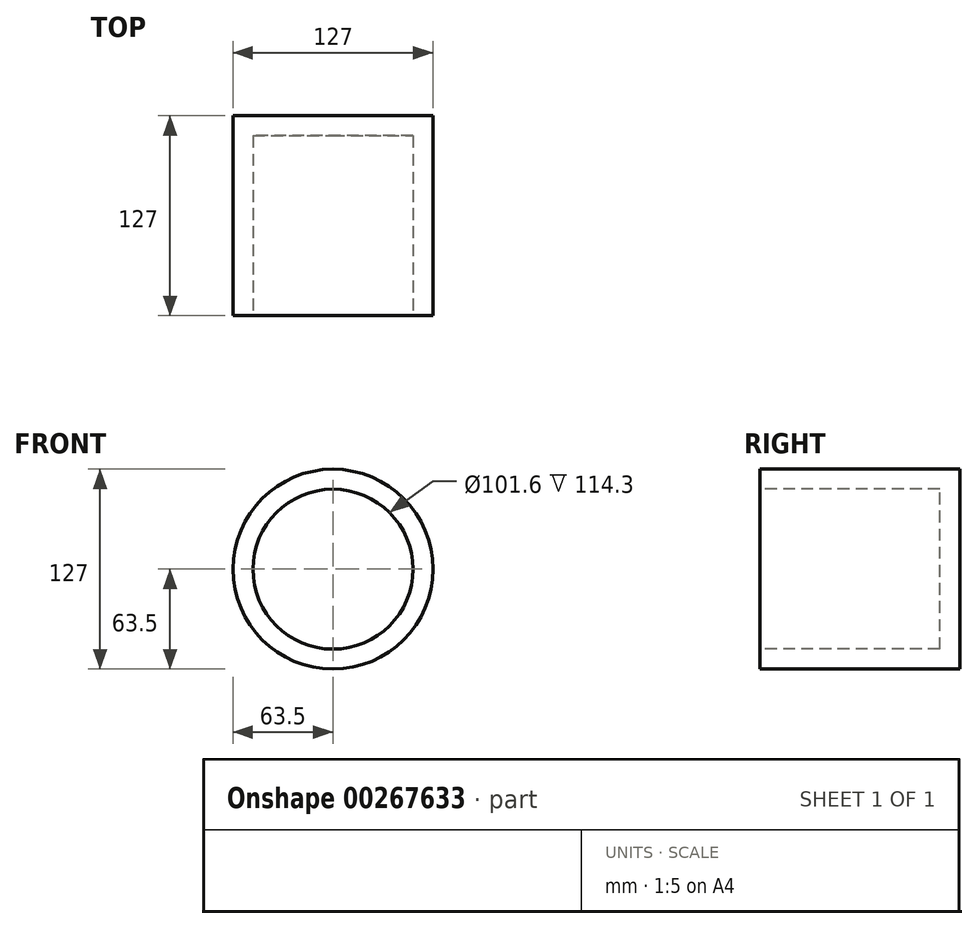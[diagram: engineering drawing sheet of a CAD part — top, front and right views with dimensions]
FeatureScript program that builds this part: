
annotation { "Feature Type Name" : "Feature", "Feature Type Description" : "" }
export const myFeature = defineFeature(function(context is Context, id is Id, definition is map)
    precondition{}
    {
        {
            var Q0;
            Q0=qCreatedBy(makeId("Front.planeOp"),FACE);
            var sketch = newSketch(context, id + "F0", { "sketchPlane" : qUnion([Q0])});
            skCircle(sketch, "E0", {"center": v(0, 0) * mm, "radius": 63.5 * mm});
            skCircle(sketch, "E1", {"center": v(0, 0) * mm, "radius": 50.8 * mm});
            skSolve(sketch);
        }
        {
            var Q0;
            Q0=makeQuery(id+"F0.imprint","IMPRINT",FACE,{"disambiguationData":[TD([[makeQuery(id+"F0.imprint","IMPRINT",EDGE,{"derivedFrom":sQuery(id+"F0.wireOp",EDGE,"E0")}),1.0]])]});
            var Q1;
            Q1=makeQuery(id+"F0.imprint","IMPRINT",FACE,{"disambiguationData":[TD([[makeQuery(id+"F0.imprint","IMPRINT",EDGE,{"derivedFrom":sQuery(id+"F0.wireOp",EDGE,"E1")}),1.0]])]});
            extrude(context, id + "F1", {"entities" : qUnion([Q0, Q1]), "oppositeDirection" : true, "depth" : 127 * mm});
        }
        {
            var Q0;
            Q0=makeQuery(id+"F0.imprint","IMPRINT",FACE,{"disambiguationData":[TD([[makeQuery(id+"F0.imprint","IMPRINT",EDGE,{"derivedFrom":sQuery(id+"F0.wireOp",EDGE,"E1")}),1.0]])]});
            extrude(context, id + "F2", {"entities" : qUnion([Q0]), "operationType" : NewBodyOperationType.REMOVE, "oppositeDirection" : true, "depth" : 114.3 * mm});
        }
    });
